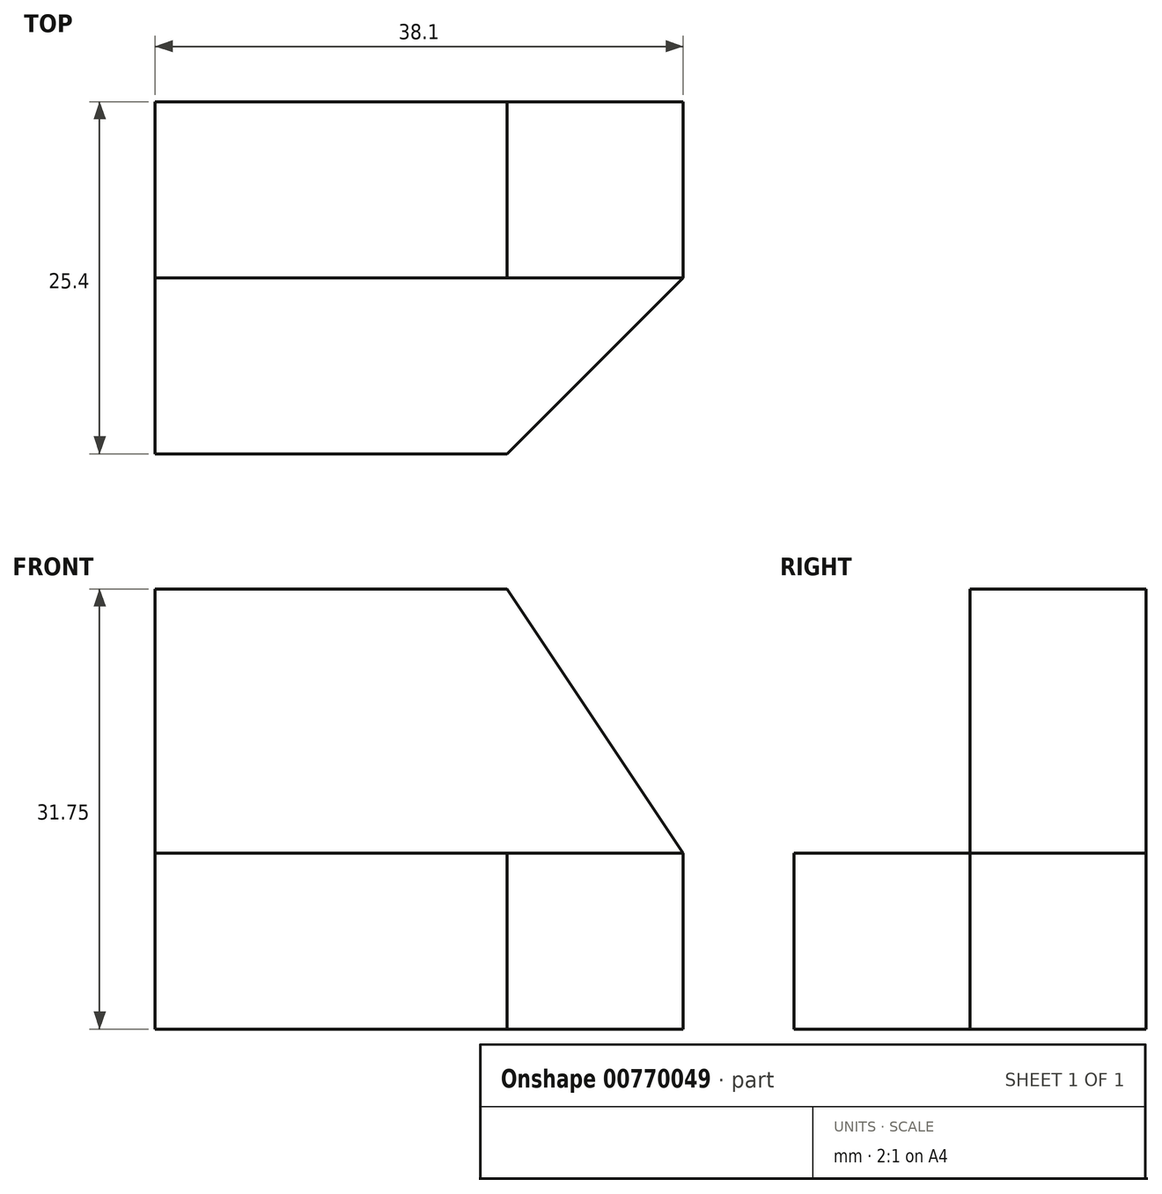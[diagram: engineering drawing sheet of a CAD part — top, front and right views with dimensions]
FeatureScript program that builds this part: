
annotation { "Feature Type Name" : "Feature", "Feature Type Description" : "" }
export const myFeature = defineFeature(function(context is Context, id is Id, definition is map)
    precondition{}
    {
        {
            var Q0;
            Q0=qCreatedBy(makeId("Front.planeOp"),FACE);
            var sketch = newSketch(context, id + "F0", { "sketchPlane" : qUnion([Q0])});
            skLineSegment(sketch, "E0", {"start": v(0, 0) * mm, "end": v(38.1, 0) * mm});
            skLineSegment(sketch, "E1", {"start": v(38.1, 0) * mm, "end": v(38.1, 31.75) * mm});
            skLineSegment(sketch, "E2", {"start": v(38.1, 31.75) * mm, "end": v(0, 31.75) * mm});
            skLineSegment(sketch, "E3", {"start": v(0, 31.75) * mm, "end": v(0, 0) * mm});
            skSolve(sketch);
        }
        {
            var Q0;
            Q0=makeQuery(id+"F0.imprint","IMPRINT",FACE,{"disambiguationData":[TD([[makeQuery(id+"F0.imprint","IMPRINT",EDGE,{"derivedFrom":sQuery(id+"F0.wireOp",EDGE,"E0")}),1.0]])]});
            extrude(context, id + "F1", {"entities" : qUnion([Q0]), "depth" : 25.4 * mm, "offsetDistance" : 25.4 * mm});
        }
        {
            var Q0;
            Q0=makeQuery(id+"F1.opExtrude","CAP_FACE",FACE,{"disambiguationData":[OSD([sQuery(id+"F0.wireOp",EDGE,"E0"),sQuery(id+"F0.wireOp",EDGE,"E1"),sQuery(id+"F0.wireOp",EDGE,"E2"),sQuery(id+"F0.wireOp",EDGE,"E3")])],"isStart":false});
            var sketch = newSketch(context, id + "F2", { "sketchPlane" : qUnion([Q0])});
            skLineSegment(sketch, "E4", {"start": v(0, 0) * mm, "end": v(0, 12.7) * mm});
            skLineSegment(sketch, "E5", {"start": v(0, 12.7) * mm, "end": v(38.1, 12.7) * mm});
            skLineSegment(sketch, "E6", {"start": v(38.1, 12.7) * mm, "end": v(38.1, 31.75) * mm});
            skLineSegment(sketch, "E7", {"start": v(38.1, 31.75) * mm, "end": v(0, 31.75) * mm});
            skLineSegment(sketch, "E8", {"start": v(0, 31.75) * mm, "end": v(0, 12.7) * mm});
            skSolve(sketch);
        }
        {
            var Q0;
            Q0=makeQuery(id+"F2.imprint","IMPRINT",FACE,{"disambiguationData":[TD([[makeQuery(id+"F2.imprint","IMPRINT",EDGE,{"derivedFrom":sQuery(id+"F2.wireOp",EDGE,"E5")}),1.0]])]});
            extrude(context, id + "F3", {"entities" : qUnion([Q0]), "operationType" : NewBodyOperationType.REMOVE, "oppositeDirection" : true, "depth" : 12.7 * mm, "offsetDistance" : 25.4 * mm});
        }
        {
            var Q0;
            Q0=makeQuery(id+"F3.boolean.opBoolean","COPY",FACE,{"derivedFrom":makeQuery(id+"F3.opExtrude","CAP_FACE",FACE,{"disambiguationData":[OSD([sQuery(id+"F2.wireOp",EDGE,"E5"),sQuery(id+"F2.wireOp",EDGE,"E6"),sQuery(id+"F2.wireOp",EDGE,"E7"),sQuery(id+"F2.wireOp",EDGE,"E8")])],"isStart":false})});
            var sketch = newSketch(context, id + "F4", { "sketchPlane" : qUnion([Q0])});
            skLineSegment(sketch, "E9", {"start": v(0, 31.75) * mm, "end": v(25.4, 31.75) * mm});
            skLineSegment(sketch, "E10", {"start": v(25.4, 31.75) * mm, "end": v(38.1, 12.7) * mm});
            skLineSegment(sketch, "E11", {"start": v(38.1, 12.7) * mm, "end": v(38.1, 31.75) * mm});
            skLineSegment(sketch, "E12", {"start": v(38.1, 31.75) * mm, "end": v(25.4, 31.75) * mm});
            skSolve(sketch);
        }
        {
            var Q0;
            Q0=makeQuery(id+"F4.imprint","IMPRINT",FACE,{"disambiguationData":[TD([[makeQuery(id+"F4.imprint","IMPRINT",EDGE,{"derivedFrom":sQuery(id+"F4.wireOp",EDGE,"E10")}),1.0]])]});
            extrude(context, id + "F5", {"entities" : qUnion([Q0]), "operationType" : NewBodyOperationType.REMOVE, "oppositeDirection" : true, "depth" : 25.4 * mm, "offsetDistance" : 25.4 * mm});
        }
        {
            var Q0;
            Q0=makeQuery(id+"F3.boolean.opBoolean","COPY",FACE,{"derivedFrom":makeQuery(id+"F3.opExtrude","SWEPT_FACE",FACE,{"disambiguationData":[OSD([sQuery(id+"F2.wireOp",EDGE,"E5")])]})});
            var sketch = newSketch(context, id + "F6", { "sketchPlane" : qUnion([Q0])});
            skLineSegment(sketch, "E13", {"start": v(0, -25.4) * mm, "end": v(25.4, -25.4) * mm});
            skLineSegment(sketch, "E14", {"start": v(25.4, -25.4) * mm, "end": v(38.1, -12.7) * mm});
            skLineSegment(sketch, "E15", {"start": v(38.1, -12.7) * mm, "end": v(38.1, -25.4) * mm});
            skLineSegment(sketch, "E16", {"start": v(38.1, -25.4) * mm, "end": v(25.4, -25.4) * mm});
            skSolve(sketch);
        }
        {
            var Q0;
            Q0=makeQuery(id+"F6.imprint","IMPRINT",FACE,{"disambiguationData":[TD([[makeQuery(id+"F6.imprint","IMPRINT",EDGE,{"derivedFrom":sQuery(id+"F6.wireOp",EDGE,"E14")}),-1.0]])]});
            extrude(context, id + "F7", {"entities" : qUnion([Q0]), "operationType" : NewBodyOperationType.REMOVE, "oppositeDirection" : true, "depth" : 25.4 * mm, "offsetDistance" : 25.4 * mm});
        }
    });
